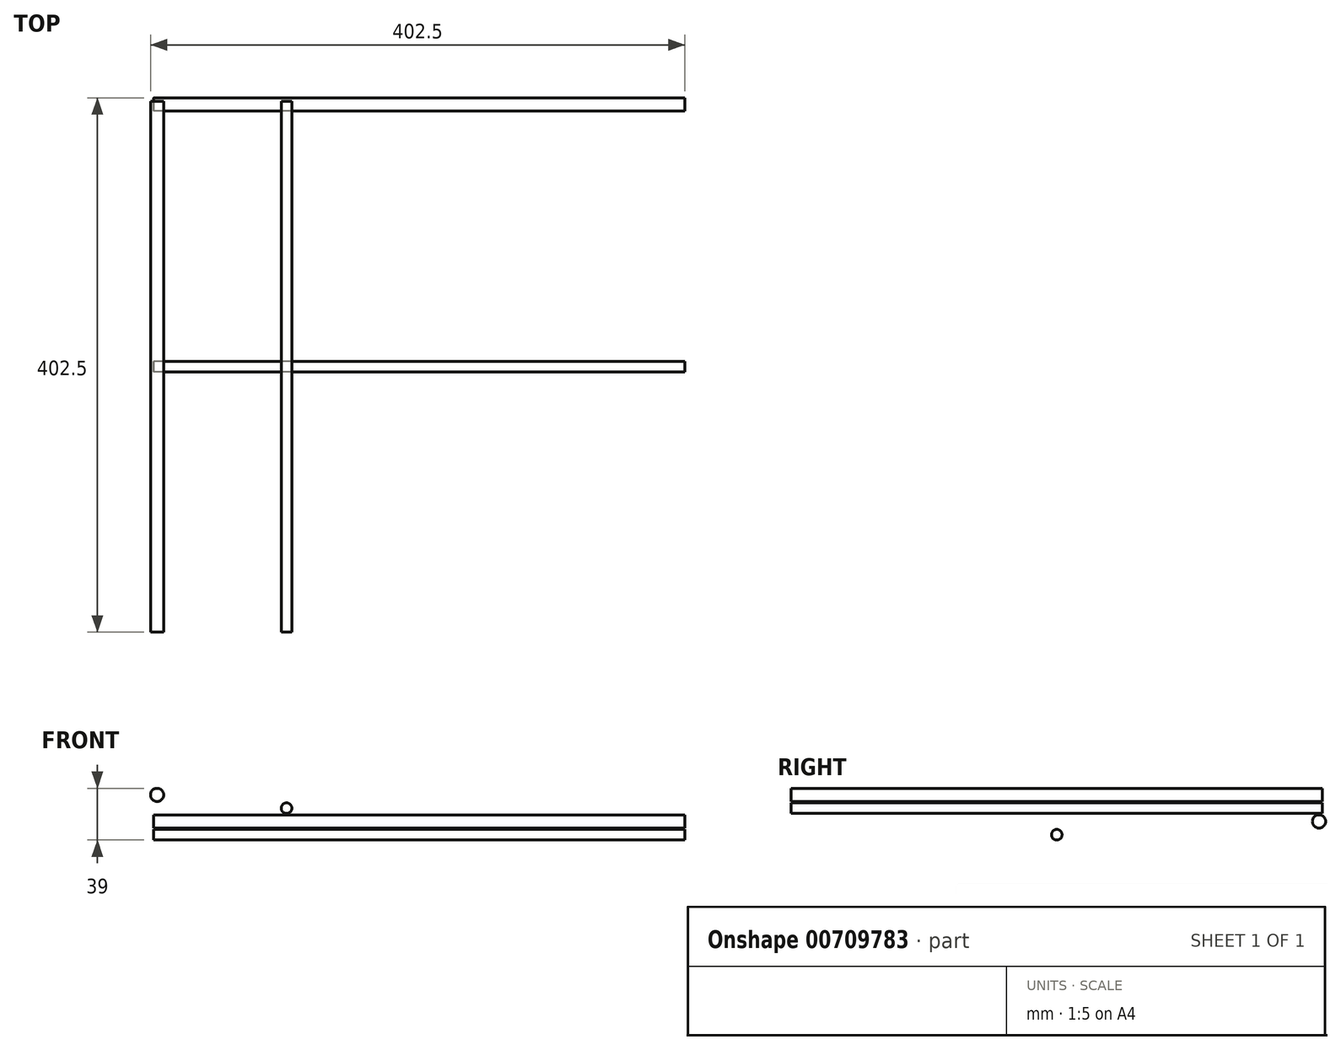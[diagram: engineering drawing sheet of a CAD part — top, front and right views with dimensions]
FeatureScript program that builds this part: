
annotation { "Feature Type Name" : "Feature", "Feature Type Description" : "" }
export const myFeature = defineFeature(function(context is Context, id is Id, definition is map)
    precondition{}
    {
        {
            var Q0;
            Q0=qCreatedBy(makeId("Front.planeOp"),FACE);
            var sketch = newSketch(context, id + "F0", { "sketchPlane" : qUnion([Q0])});
            skCircle(sketch, "E0", {"center": v(-197.5, 20) * mm, "radius": 5 * mm});
            skCircle(sketch, "E1", {"center": v(197.5, 20) * mm, "radius": 5 * mm});
            skCircle(sketch, "E2", {"center": v(-197.5, -20) * mm, "radius": 5 * mm});
            skCircle(sketch, "E3", {"center": v(197.5, -20) * mm, "radius": 5 * mm});
            skLineSegment(sketch, "E4", {"start": v(0, 0) * mm, "end": v(-75.4, 0) * mm, "construction": true});
            skLineSegment(sketch, "E5", {"start": v(0, 0) * mm, "end": v(0, 24.91) * mm, "construction": true});
            skSolve(sketch);
        }
        {
            var Q0;
            Q0=makeQuery(id+"F0.imprint","IMPRINT",FACE,{"disambiguationData":[TD([[makeQuery(id+"F0.imprint","IMPRINT",EDGE,{"derivedFrom":sQuery(id+"F0.wireOp",EDGE,"E0")}),1.0]])]});
            var Q1;
            Q1=makeQuery(id+"F0.imprint","IMPRINT",FACE,{"disambiguationData":[TD([[makeQuery(id+"F0.imprint","IMPRINT",EDGE,{"derivedFrom":sQuery(id+"F0.wireOp",EDGE,"E2")}),1.0]])]});
            var Q2;
            Q2=makeQuery(id+"F0.imprint","IMPRINT",FACE,{"disambiguationData":[TD([[makeQuery(id+"F0.imprint","IMPRINT",EDGE,{"derivedFrom":sQuery(id+"F0.wireOp",EDGE,"E3")}),1.0]])]});
            var Q3;
            Q3=makeQuery(id+"F0.imprint","IMPRINT",FACE,{"disambiguationData":[TD([[makeQuery(id+"F0.imprint","IMPRINT",EDGE,{"derivedFrom":sQuery(id+"F0.wireOp",EDGE,"E1")}),1.0]])]});
            extrude(context, id + "F1", {"entities" : qUnion([Q0, Q1, Q2, Q3]), "endBound" : BoundingType.SYMMETRIC, "depth" : 400 * mm, "offsetDistance" : 25 * mm});
        }
        {
            var Q0;
            Q0=qCreatedBy(makeId("Right.planeOp"),FACE);
            var sketch = newSketch(context, id + "F2", { "sketchPlane" : qUnion([Q0])});
            skCircle(sketch, "E6", {"center": v(-197.5, 0) * mm, "radius": 5 * mm});
            skCircle(sketch, "E7", {"center": v(197.5, 0) * mm, "radius": 5 * mm});
            skSolve(sketch);
        }
        {
            var Q0;
            Q0=makeQuery(id+"F2.imprint","IMPRINT",FACE,{"disambiguationData":[TD([[makeQuery(id+"F2.imprint","IMPRINT",EDGE,{"derivedFrom":sQuery(id+"F2.wireOp",EDGE,"E6")}),1.0]])]});
            var Q1;
            Q1=makeQuery(id+"F2.imprint","IMPRINT",FACE,{"disambiguationData":[TD([[makeQuery(id+"F2.imprint","IMPRINT",EDGE,{"derivedFrom":sQuery(id+"F2.wireOp",EDGE,"E7")}),1.0]])]});
            extrude(context, id + "F3", {"entities" : qUnion([Q0, Q1]), "endBound" : BoundingType.SYMMETRIC, "depth" : 400 * mm, "offsetDistance" : 25 * mm});
        }
        {
            var Q0;
            Q0=qCreatedBy(makeId("Front.planeOp"),FACE);
            var sketch = newSketch(context, id + "F4", { "sketchPlane" : qUnion([Q0])});
            skCircle(sketch, "E8", {"center": v(-100, 10) * mm, "radius": 4 * mm});
            skCircle(sketch, "E9", {"center": v(100, 10) * mm, "radius": 4 * mm});
            skSolve(sketch);
        }
        {
            var Q0;
            Q0=makeQuery(id+"F4.imprint","IMPRINT",FACE,{"disambiguationData":[TD([[makeQuery(id+"F4.imprint","IMPRINT",EDGE,{"derivedFrom":sQuery(id+"F4.wireOp",EDGE,"E8")}),1.0]])]});
            var Q1;
            Q1=makeQuery(id+"F4.imprint","IMPRINT",FACE,{"disambiguationData":[TD([[makeQuery(id+"F4.imprint","IMPRINT",EDGE,{"derivedFrom":sQuery(id+"F4.wireOp",EDGE,"E9")}),1.0]])]});
            extrude(context, id + "F5", {"entities" : qUnion([Q0, Q1]), "endBound" : BoundingType.SYMMETRIC, "depth" : 400 * mm, "offsetDistance" : 25 * mm});
        }
        {
            var Q0;
            Q0=qCreatedBy(makeId("Right.planeOp"),FACE);
            var sketch = newSketch(context, id + "F6", { "sketchPlane" : qUnion([Q0])});
            skCircle(sketch, "E10", {"center": v(0, -10) * mm, "radius": 4 * mm});
            skSolve(sketch);
        }
        {
            var Q0;
            Q0=makeQuery(id+"F6.imprint","IMPRINT",FACE,{"disambiguationData":[TD([[makeQuery(id+"F6.imprint","IMPRINT",EDGE,{"derivedFrom":sQuery(id+"F6.wireOp",EDGE,"E10")}),1.0]])]});
            extrude(context, id + "F7", {"entities" : qUnion([Q0]), "endBound" : BoundingType.SYMMETRIC, "depth" : 400 * mm, "offsetDistance" : 25 * mm});
        }
        {
            var Q0;
            Q0=makeQuery(id+"F5.opExtrude","SWEPT_BODY",BODY,{"disambiguationData":[OSD([sQuery(id+"F4.wireOp",EDGE,"E9")])]});
            var Q1;
            Q1=makeQuery(id+"F1.opExtrude","SWEPT_BODY",BODY,{"disambiguationData":[OSD([sQuery(id+"F0.wireOp",EDGE,"E1")])]});
            var Q2;
            Q2=makeQuery(id+"F1.opExtrude","SWEPT_BODY",BODY,{"disambiguationData":[OSD([sQuery(id+"F0.wireOp",EDGE,"E3")])]});
            var Q3;
            Q3=makeQuery(id+"F1.opExtrude","SWEPT_BODY",BODY,{"disambiguationData":[OSD([sQuery(id+"F0.wireOp",EDGE,"E2")])]});
            var Q4;
            Q4=makeQuery(id+"F3.opExtrude","SWEPT_BODY",BODY,{"disambiguationData":[OSD([sQuery(id+"F2.wireOp",EDGE,"E6")])]});
            deleteBodies(context, id + "F8", {"entities" : qUnion([Q0, Q1, Q2, Q3, Q4])});
        }
    });
